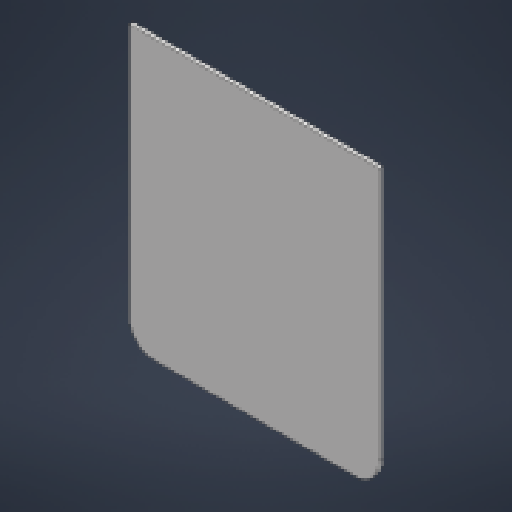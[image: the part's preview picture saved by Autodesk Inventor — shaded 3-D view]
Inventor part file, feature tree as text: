
AUTODESK INVENTOR PART (.ipt)
format: ipt  version: 2025 (Build 290162000, 162)  size: 171,008 bytes
history: native  units: mm
features: extrude x1, fillet x1, sketch x1
ambient origin geometry x8: Origin, YZ Plane, XZ Plane, XY Plane, X Axis, Y Axis, Z Axis, Center Point
bodies: 实体1 (feature_tree)
feature tree (3):
  extrude  "拉伸1"  Depth=78.0mm
  fillet  "圆角1"  Radius=1.0mm
  sketch  "草图1"  dims[d0=70.0mm d1=78.0mm d2=1.0mm d3=0.0mm d4=7.0mm]
